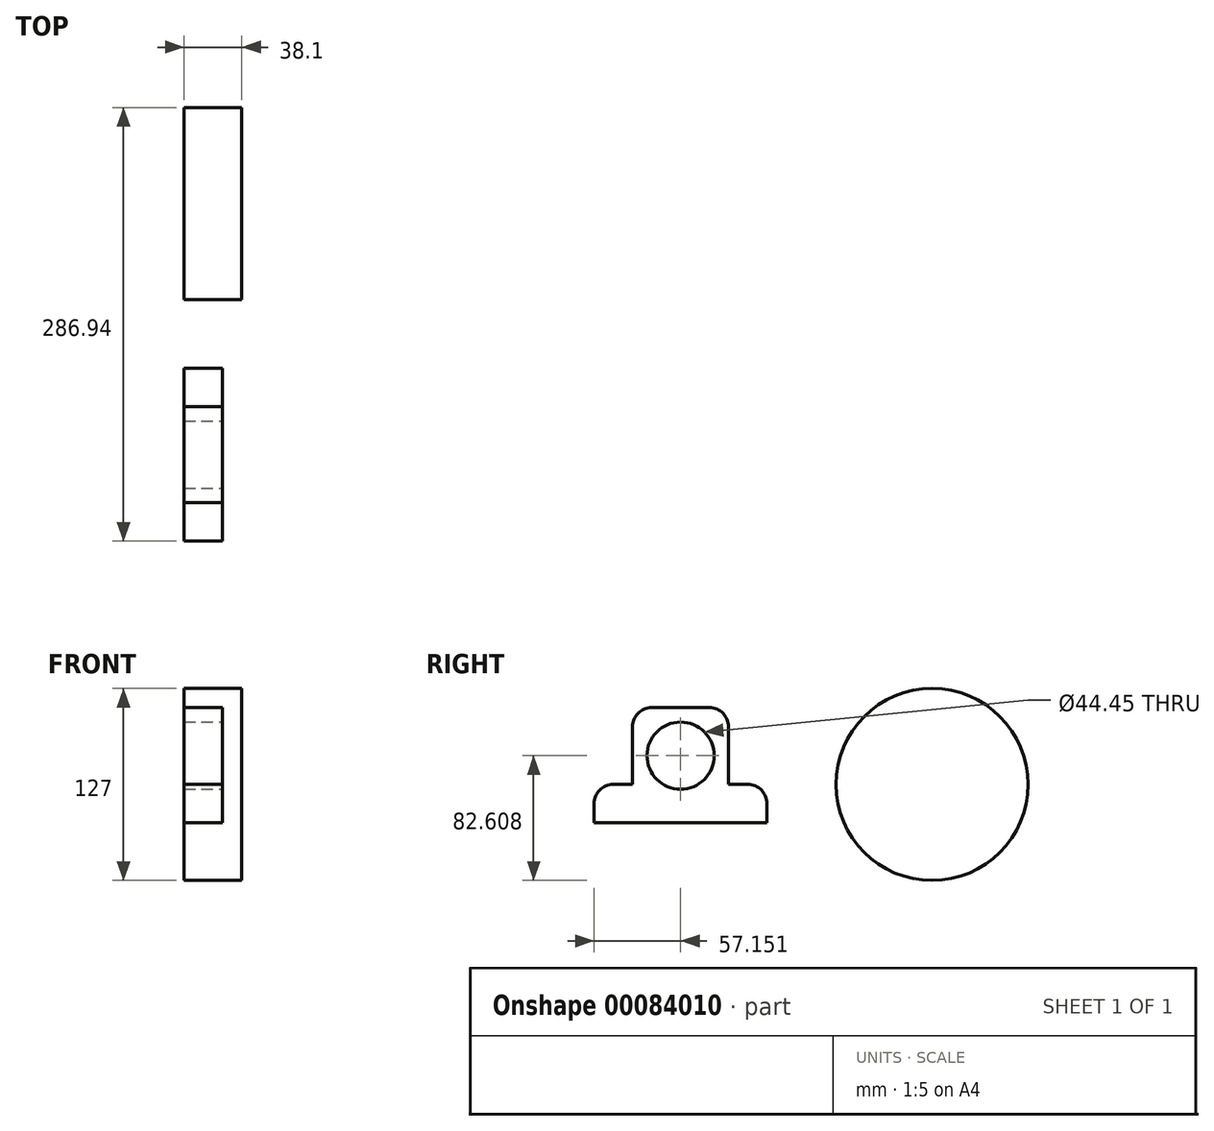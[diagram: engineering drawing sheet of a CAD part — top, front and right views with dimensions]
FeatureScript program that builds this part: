
annotation { "Feature Type Name" : "Feature", "Feature Type Description" : "" }
export const myFeature = defineFeature(function(context is Context, id is Id, definition is map)
    precondition{}
    {
        {
            var Q0;
            Q0=qCreatedBy(makeId("Right.planeOp"),FACE);
            var sketch = newSketch(context, id + "F0", { "sketchPlane" : qUnion([Q0])});
            skCircle(sketch, "E0", {"center": v(0, 0) * mm, "radius": 63.5 * mm});
            skSolve(sketch);
        }
        {
            var Q0;
            Q0=makeQuery(id+"F0.imprint","IMPRINT",FACE,{"disambiguationData":[TD([[makeQuery(id+"F0.imprint","IMPRINT",EDGE,{"derivedFrom":sQuery(id+"F0.wireOp",EDGE,"E0")}),1.0]])]});
            extrude(context, id + "F1", {"entities" : qUnion([Q0]), "depth" : 38.1 * mm});
        }
        {
            var Q0;
            Q0=qCreatedBy(makeId("Right.planeOp"),FACE);
            var sketch = newSketch(context, id + "F2", { "sketchPlane" : qUnion([Q0])});
            skLineSegment(sketch, "E1.bottom", {"start": v(-198.04, -25.34) * mm, "end": v(-134.54, -25.34) * mm});
            skLineSegment(sketch, "E1.top", {"start": v(-198.04, 50.86) * mm, "end": v(-134.54, 50.86) * mm});
            skLineSegment(sketch, "E1.left", {"start": v(-198.04, -25.34) * mm, "end": v(-198.04, 50.86) * mm});
            skLineSegment(sketch, "E1.right", {"start": v(-134.54, -25.34) * mm, "end": v(-134.54, 50.86) * mm});
            skSolve(sketch);
        }
        {
            var Q0;
            Q0=makeQuery(id+"F2.imprint","IMPRINT",FACE,{"disambiguationData":[TD([[makeQuery(id+"F2.imprint","IMPRINT",EDGE,{"derivedFrom":sQuery(id+"F2.wireOp",EDGE,"E1.bottom")}),1.0]])]});
            extrude(context, id + "F3", {"entities" : qUnion([Q0]), "depth" : 25.4 * mm});
        }
        {
            var Q0;
            Q0=makeQuery(id+"F3.opExtrude","CAP_FACE",FACE,{"disambiguationData":[OSD([sQuery(id+"F2.wireOp",EDGE,"E1.bottom"),sQuery(id+"F2.wireOp",EDGE,"E1.top"),sQuery(id+"F2.wireOp",EDGE,"E1.left"),sQuery(id+"F2.wireOp",EDGE,"E1.right")])],"isStart":false});
            var sketch = newSketch(context, id + "F4", { "sketchPlane" : qUnion([Q0])});
            skCircle(sketch, "E2", {"center": v(-166.29, 19.1) * mm, "radius": 9.53 * mm});
            skSolve(sketch);
        }
        {
            var Q0;
            Q0=sQuery(id+"F4.wireOp",VERTEX,"E2.center");
            var Q1;
            Q1=makeQuery(id+"F3.opExtrude","SWEPT_BODY",BODY,{"disambiguationData":[OSD([sQuery(id+"F2.wireOp",EDGE,"E1.bottom"),sQuery(id+"F2.wireOp",EDGE,"E1.top"),sQuery(id+"F2.wireOp",EDGE,"E1.left"),sQuery(id+"F2.wireOp",EDGE,"E1.right")])]});
            hole(context, id + "F5", {"style" : HoleStyle.SIMPLE, "endStyle" : HoleEndStyle.THROUGH, "holeDiameter" : 44.45 * mm, "locations" : qUnion([Q0]), "scope" : qUnion([Q1]), "isTappedThrough" : true});
        }
        {
            var Q0;
            Q0=makeQuery(id+"F3.opExtrude","SWEPT_FACE",FACE,{"disambiguationData":[OSD([sQuery(id+"F2.wireOp",EDGE,"E1.left")])]});
            var sketch = newSketch(context, id + "F6", { "sketchPlane" : qUnion([Q0])});
            skLineSegment(sketch, "E3.bottom", {"start": v(0, -25.34) * mm, "end": v(25.4, -25.34) * mm});
            skLineSegment(sketch, "E3.top", {"start": v(0, 0.06) * mm, "end": v(25.4, 0.06) * mm});
            skLineSegment(sketch, "E3.left", {"start": v(0, -25.34) * mm, "end": v(0, 0.06) * mm});
            skLineSegment(sketch, "E3.right", {"start": v(25.4, -25.34) * mm, "end": v(25.4, 0.06) * mm});
            skSolve(sketch);
        }
        {
            var Q0;
            Q0=makeQuery(id+"F3.opExtrude","SWEPT_FACE",FACE,{"disambiguationData":[OSD([sQuery(id+"F2.wireOp",EDGE,"E1.right")])]});
            var sketch = newSketch(context, id + "F7", { "sketchPlane" : qUnion([Q0])});
            skLineSegment(sketch, "E4.bottom", {"start": v(-25.4, -25.34) * mm, "end": v(0, -25.34) * mm});
            skLineSegment(sketch, "E4.top", {"start": v(-25.4, 0.06) * mm, "end": v(0, 0.06) * mm});
            skLineSegment(sketch, "E4.left", {"start": v(-25.4, -25.34) * mm, "end": v(-25.4, 0.06) * mm});
            skLineSegment(sketch, "E4.right", {"start": v(0, -25.34) * mm, "end": v(0, 0.06) * mm});
            skSolve(sketch);
        }
        {
            var Q0;
            Q0=makeQuery(id+"F7.imprint","IMPRINT",FACE,{"disambiguationData":[TD([[makeQuery(id+"F7.imprint","IMPRINT",EDGE,{"derivedFrom":sQuery(id+"F7.wireOp",EDGE,"E4.bottom")}),1.0]])]});
            extrude(context, id + "F8", {"entities" : qUnion([Q0]), "operationType" : NewBodyOperationType.ADD, "depth" : 25.4 * mm});
        }
        {
            var Q0;
            Q0=makeQuery(id+"F6.imprint","IMPRINT",FACE,{"disambiguationData":[TD([[makeQuery(id+"F6.imprint","IMPRINT",EDGE,{"derivedFrom":sQuery(id+"F6.wireOp",EDGE,"E3.bottom")}),-1.0]])]});
            extrude(context, id + "F9", {"entities" : qUnion([Q0]), "operationType" : NewBodyOperationType.ADD, "depth" : 25.4 * mm});
        }
        {
            var Q0;
            Q0=makeQuery(id+"F9.opExtrude","CAP_EDGE",EDGE,{"disambiguationData":[OSD([sQuery(id+"F6.wireOp",EDGE,"E3.top")])],"isStart":false});
            var Q1;
            Q1=makeQuery(id+"F9.opExtrude","CAP_EDGE",EDGE,{"disambiguationData":[OSD([sQuery(id+"F6.wireOp",EDGE,"E3.top")])],"isStart":true});
            var Q2;
            Q2=makeQuery(id+"F3.opExtrude","SWEPT_EDGE",EDGE,{"disambiguationData":[OSD([sQuery(id+"F2.wireOp",EDGE,"E1.top"),sQuery(id+"F2.wireOp",EDGE,"E1.left")])]});
            var Q3;
            Q3=makeQuery(id+"F3.opExtrude","SWEPT_EDGE",EDGE,{"disambiguationData":[OSD([sQuery(id+"F2.wireOp",EDGE,"E1.top"),sQuery(id+"F2.wireOp",EDGE,"E1.right")])]});
            var Q4;
            Q4=makeQuery(id+"F8.opExtrude","CAP_EDGE",EDGE,{"disambiguationData":[OSD([sQuery(id+"F7.wireOp",EDGE,"E4.top")])],"isStart":true});
            var Q5;
            Q5=makeQuery(id+"F8.opExtrude","CAP_EDGE",EDGE,{"disambiguationData":[OSD([sQuery(id+"F7.wireOp",EDGE,"E4.top")])],"isStart":false});
            fillet(context, id + "F10", {"entities" : qUnion([Q0, Q1, Q2, Q3, Q4, Q5]), "radius" : 12.7 * mm, "tangentPropagation" : true, "allowEdgeOverflow" : false});
        }
    });
